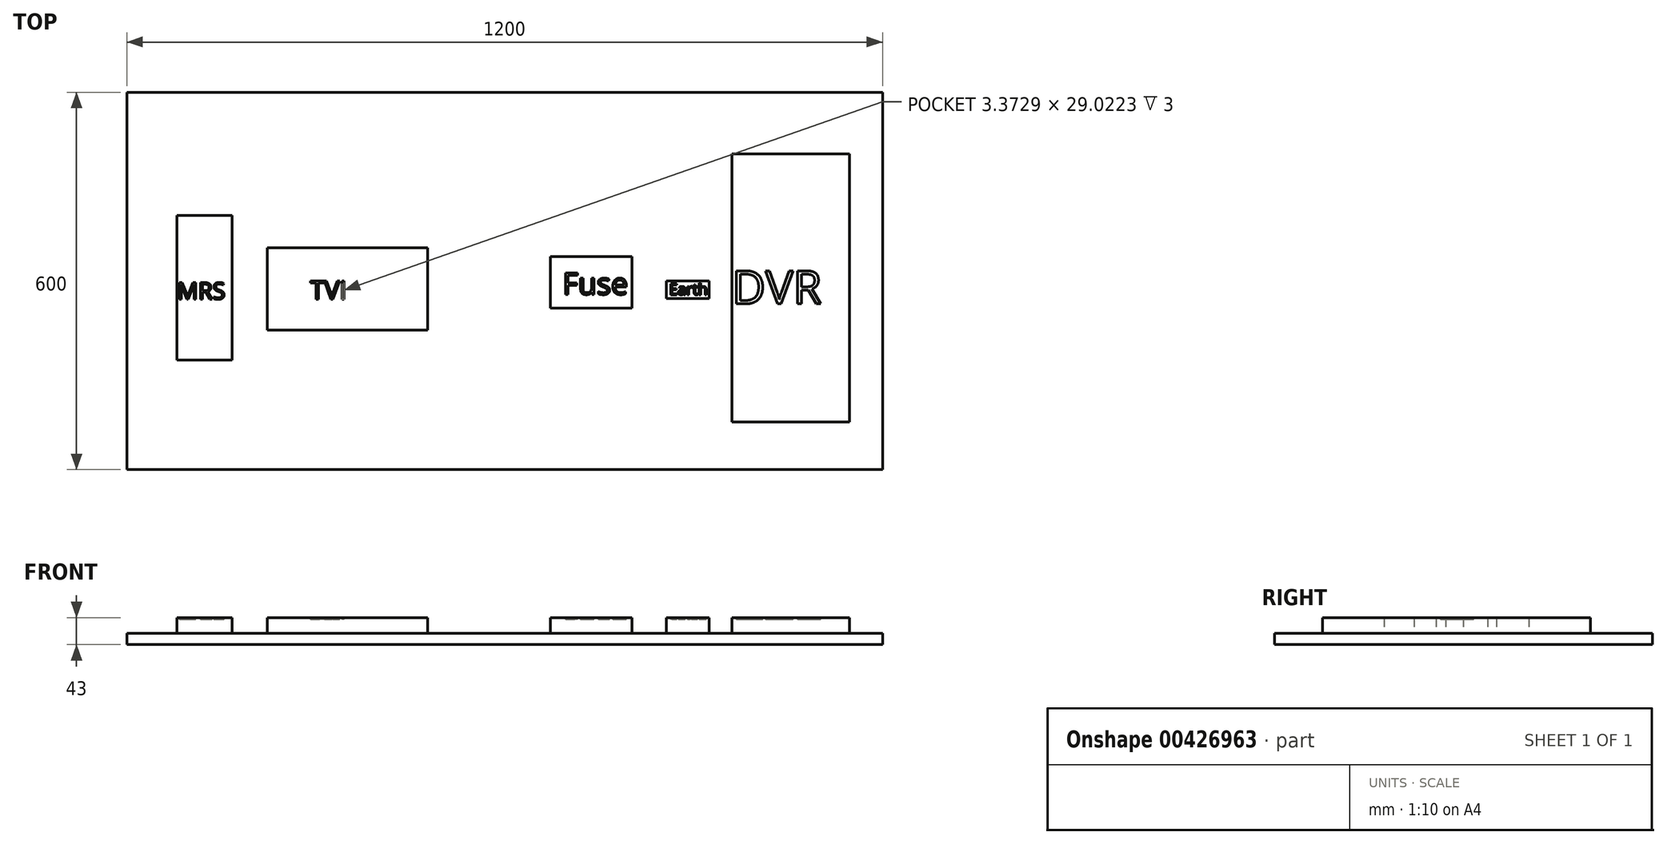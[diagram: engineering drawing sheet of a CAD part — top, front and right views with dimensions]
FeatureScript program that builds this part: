
annotation { "Feature Type Name" : "Feature", "Feature Type Description" : "" }
export const myFeature = defineFeature(function(context is Context, id is Id, definition is map)
    precondition{}
    {
        {
            var Q0;
            Q0=qCreatedBy(makeId("Top.planeOp"),FACE);
            var sketch = newSketch(context, id + "F0", { "sketchPlane" : qUnion([Q0])});
            skLineSegment(sketch, "E0.bottom", {"start": v(600, -300) * mm, "end": v(-600, -300) * mm});
            skLineSegment(sketch, "E0.top", {"start": v(600, 300) * mm, "end": v(-600, 300) * mm});
            skLineSegment(sketch, "E0.left", {"start": v(600, -300) * mm, "end": v(600, 300) * mm});
            skLineSegment(sketch, "E0.right", {"start": v(-600, -300) * mm, "end": v(-600, 300) * mm});
            skPoint(sketch, "E0.middle", {"position": v(0, 0) * mm});
            skSolve(sketch);
        }
        {
            var Q0;
            Q0 = qSketchRegion(id + "F0", true);
            extrude(context, id + "F1", {"entities" : qUnion([Q0]), "depth" : 18 * mm});
        }
        {
            var Q0;
            Q0=makeQuery(id+"F1.opExtrude","CAP_FACE",FACE,{"disambiguationData":[OSD([sQuery(id+"F0.wireOp",EDGE,"E0.bottom"),sQuery(id+"F0.wireOp",EDGE,"E0.top"),sQuery(id+"F0.wireOp",EDGE,"E0.left"),sQuery(id+"F0.wireOp",EDGE,"E0.right")])],"isStart":false});
            var sketch = newSketch(context, id + "F2", { "sketchPlane" : qUnion([Q0])});
            skLineSegment(sketch, "E1.bottom", {"start": v(-520.33, 103.83) * mm, "end": v(-432.83, 103.83) * mm});
            skLineSegment(sketch, "E1.top", {"start": v(-520.33, -126) * mm, "end": v(-432.83, -126) * mm});
            skLineSegment(sketch, "E1.left", {"start": v(-520.33, 103.83) * mm, "end": v(-520.33, -126) * mm});
            skLineSegment(sketch, "E1.right", {"start": v(-432.83, 103.83) * mm, "end": v(-432.83, -126) * mm});
            skLineSegment(sketch, "E2.bottom", {"start": v(72.33, 38.5) * mm, "end": v(201.83, 38.5) * mm});
            skLineSegment(sketch, "E2.top", {"start": v(72.33, -43.17) * mm, "end": v(201.83, -43.17) * mm});
            skLineSegment(sketch, "E2.left", {"start": v(72.33, 38.5) * mm, "end": v(72.33, -43.17) * mm});
            skLineSegment(sketch, "E2.right", {"start": v(201.83, 38.5) * mm, "end": v(201.83, -43.17) * mm});
            skLineSegment(sketch, "E3.bottom", {"start": v(256.67, 0) * mm, "end": v(324.33, 0) * mm});
            skLineSegment(sketch, "E3.top", {"start": v(256.67, -28) * mm, "end": v(324.33, -28) * mm});
            skLineSegment(sketch, "E3.left", {"start": v(256.67, 0) * mm, "end": v(256.67, -28) * mm});
            skLineSegment(sketch, "E3.right", {"start": v(324.33, 0) * mm, "end": v(324.33, -28) * mm});
            skLineSegment(sketch, "E4.bottom", {"start": v(360.5, 201.83) * mm, "end": v(547.17, 201.83) * mm});
            skLineSegment(sketch, "E4.top", {"start": v(360.5, -224) * mm, "end": v(547.17, -224) * mm});
            skLineSegment(sketch, "E4.left", {"start": v(360.5, 201.83) * mm, "end": v(360.5, -224) * mm});
            skLineSegment(sketch, "E4.right", {"start": v(547.17, 201.83) * mm, "end": v(547.17, -224) * mm});
            skLineSegment(sketch, "E5.bottom", {"start": v(-376.83, 52.5) * mm, "end": v(-122.5, 52.5) * mm});
            skLineSegment(sketch, "E5.top", {"start": v(-376.83, -78.17) * mm, "end": v(-122.5, -78.17) * mm});
            skLineSegment(sketch, "E5.left", {"start": v(-376.83, 52.5) * mm, "end": v(-376.83, -78.17) * mm});
            skLineSegment(sketch, "E5.right", {"start": v(-122.5, 52.5) * mm, "end": v(-122.5, -78.17) * mm});
            skSolve(sketch);
        }
        {
            var Q0;
            Q0 = qSketchRegion(id + "F2", true);
            extrude(context, id + "F3", {"entities" : qUnion([Q0]), "depth" : 25 * mm});
        }
        {
            var Q0;
            Q0=makeQuery(id+"F3.opExtrude","CAP_FACE",FACE,{"disambiguationData":[OSD([sQuery(id+"F2.wireOp",EDGE,"E1.bottom"),sQuery(id+"F2.wireOp",EDGE,"E1.top"),sQuery(id+"F2.wireOp",EDGE,"E1.left"),sQuery(id+"F2.wireOp",EDGE,"E1.right")])],"isStart":false});
            var sketch = newSketch(context, id + "F4", { "sketchPlane" : qUnion([Q0])});
            skText(sketch, "E6", { "text": "MRS\n", "fontName": "OpenSans-Regular.ttf"});
            skText(sketch, "E7", { "text": "TVI", "fontName": "OpenSans-Regular.ttf"});
            skText(sketch, "E8", { "text": "Fuse", "fontName": "OpenSans-Regular.ttf"});
            skText(sketch, "E9", { "text": "Earth", "fontName": "OpenSans-Regular.ttf"});
            skPoint(sketch, "E9.firstSnap0", {"position": v(196.3, -4.24) * mm});
            skText(sketch, "E10", { "text": "DVR", "fontName": "OpenSans-Regular.ttf"});
            const initialGuessF4  = {"E6": [-0.52033, -0.029, 1, 0, 0.02661], "E7": [-0.30906, -0.02927, 1, 0, 0.02927], "E8": [0.09176, -0.0215, 1, 0, 0.03452], "E9": [0.26088, -0.02193, 1, 0, 0.01769], "E10": [0.3605, -0.03636, 1, 0, 0.05291]};
            skSetInitialGuess(sketch, initialGuessF4);
            skSolve(sketch);
        }
        {
            var Q0;
            Q0 = qSketchRegion(id + "F4", true);
            extrude(context, id + "F5", {"entities" : qUnion([Q0]), "operationType" : NewBodyOperationType.REMOVE, "oppositeDirection" : true, "depth" : 3 * mm});
        }
    });
